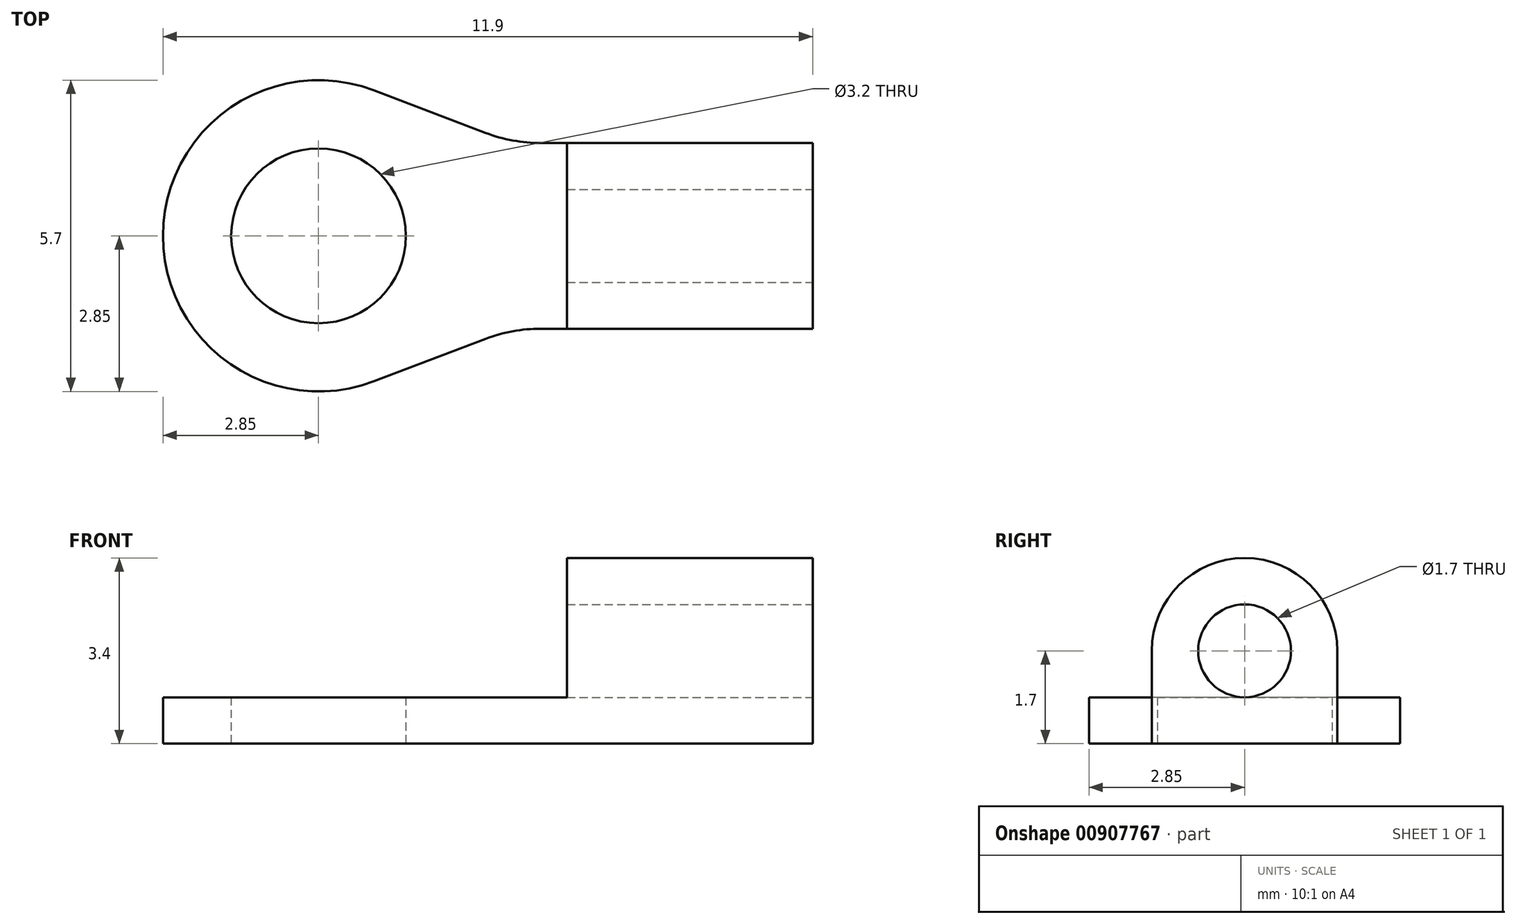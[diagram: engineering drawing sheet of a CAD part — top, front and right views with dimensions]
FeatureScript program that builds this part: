
annotation { "Feature Type Name" : "Feature", "Feature Type Description" : "" }
export const myFeature = defineFeature(function(context is Context, id is Id, definition is map)
    precondition{}
    {
        {
            var Q0;
            Q0=qCreatedBy(makeId("Top.planeOp"),FACE);
            var sketch = newSketch(context, id + "F0", { "sketchPlane" : qUnion([Q0])});
            skLineSegment(sketch, "E0.left", {"start": v(0, 2.85) * mm, "end": v(0, 2.85) * mm});
            skLineSegment(sketch, "E0.right", {"start": v(11.9, 1.15) * mm, "end": v(11.9, 4.55) * mm});
            skPoint(sketch, "E1.visualSharp", {"position": v(0, 5.7) * mm});
            skArc(sketch, "E1.filletArc", {"start": v(2.85, 5.7) * mm, "mid": v(0.83, 4.87) * mm, "end": v(0, 2.85) * mm});
            skPoint(sketch, "E2.visualSharp", {"position": v(0, 0) * mm});
            skArc(sketch, "E2.filletArc", {"start": v(0, 2.85) * mm, "mid": v(0.83, 0.83) * mm, "end": v(2.85, 0) * mm});
            skLineSegment(sketch, "E3.bottom", {"start": v(6.92, 4.55) * mm, "end": v(11.9, 4.55) * mm});
            skLineSegment(sketch, "E3.top", {"start": v(6.92, 1.15) * mm, "end": v(11.9, 1.15) * mm});
            skPoint(sketch, "E3.middle", {"position": v(11.9, 2.85) * mm});
            skArc(sketch, "E4", {"start": v(3.86, 5.51) * mm, "mid": v(0, 2.85) * mm, "end": v(3.86, 0.19) * mm});
            skCircle(sketch, "E5", {"center": v(2.85, 2.85) * mm, "radius": 1.6 * mm});
            skLineSegment(sketch, "E6", {"start": v(5.91, 4.74) * mm, "end": v(3.86, 5.51) * mm});
            skLineSegment(sketch, "E7", {"start": v(5.91, 0.96) * mm, "end": v(3.86, 0.19) * mm});
            skPoint(sketch, "E8.visualSharp", {"position": v(6.4, 4.55) * mm});
            skArc(sketch, "E8.filletArc", {"start": v(5.91, 4.74) * mm, "mid": v(6.4, 4.6) * mm, "end": v(6.92, 4.55) * mm});
            skPoint(sketch, "E9.visualSharp", {"position": v(6.4, 1.15) * mm});
            skArc(sketch, "E9.filletArc", {"start": v(6.92, 1.15) * mm, "mid": v(6.4, 1.1) * mm, "end": v(5.91, 0.96) * mm});
            skPoint(sketch, "E10.orphan", {"position": v(16.4, 4.55) * mm});
            skPoint(sketch, "E11.orphan", {"position": v(16.4, 1.15) * mm});
            skPoint(sketch, "E12.orphan", {"position": v(11.9, 0) * mm});
            skPoint(sketch, "E13.orphan", {"position": v(11.9, 5.7) * mm});
            skPoint(sketch, "E14.orphan", {"position": v(7.4, 4.55) * mm});
            skPoint(sketch, "E15.start.orphan", {"position": v(7.4, 1.15) * mm});
            skSolve(sketch);
        }
        {
            var Q0;
            Q0 = qSketchRegion(id + "F0", true);
            extrude(context, id + "F1", {"entities" : qUnion([Q0]), "depth" : 0.85 * mm, "offsetDistance" : 25 * mm});
        }
        {
            var Q0;
            Q0=makeQuery(id+"F1.opExtrude","CAP_FACE",FACE,{"disambiguationData":[OSD([sQuery(id+"F0.wireOp",EDGE,"E0.right"),sQuery(id+"F0.wireOp",EDGE,"E3.bottom"),sQuery(id+"F0.wireOp",EDGE,"E3.top"),sQuery(id+"F0.wireOp",EDGE,"E4"),sQuery(id+"F0.wireOp",EDGE,"E5"),sQuery(id+"F0.wireOp",EDGE,"E6"),sQuery(id+"F0.wireOp",EDGE,"E7"),sQuery(id+"F0.wireOp",EDGE,"E8.filletArc"),sQuery(id+"F0.wireOp",EDGE,"E9.filletArc")])],"isStart":false});
            var sketch = newSketch(context, id + "F2", { "sketchPlane" : qUnion([Q0])});
            skLineSegment(sketch, "E16.bottom", {"start": v(11.9, 4.55) * mm, "end": v(7.4, 4.55) * mm});
            skLineSegment(sketch, "E16.top", {"start": v(11.9, 1.15) * mm, "end": v(7.4, 1.15) * mm});
            skLineSegment(sketch, "E16.left", {"start": v(11.9, 4.55) * mm, "end": v(11.9, 1.15) * mm});
            skLineSegment(sketch, "E16.right", {"start": v(7.4, 4.55) * mm, "end": v(7.4, 1.15) * mm});
            skSolve(sketch);
        }
        {
            var Q0;
            Q0=makeQuery(id+"F2.imprint","IMPRINT",FACE,{"disambiguationData":[TD([[makeQuery(id+"F2.imprint","IMPRINT",EDGE,{"derivedFrom":sQuery(id+"F2.wireOp",EDGE,"E16.bottom")}),-1.0]])]});
            extrude(context, id + "F3", {"entities" : qUnion([Q0]), "operationType" : NewBodyOperationType.ADD, "depth" : 2.55 * mm, "offsetDistance" : 25 * mm});
        }
        {
            var Q0;
            Q0=makeQuery(id+"F3.opExtrude","CAP_EDGE",EDGE,{"disambiguationData":[OSD([sQuery(id+"F2.wireOp",EDGE,"E16.bottom")])],"isStart":false});
            var Q1;
            Q1=makeQuery(id+"F3.opExtrude","CAP_EDGE",EDGE,{"disambiguationData":[OSD([sQuery(id+"F2.wireOp",EDGE,"E16.top")])],"isStart":false});
            fillet(context, id + "F4", {"entities" : qUnion([Q0, Q1]), "radius" : 1.7 * mm, "tangentPropagation" : true, "allowEdgeOverflow" : false});
        }
        {
            var Q0;
            Q0=makeQuery(id+"F3.boolean.opBoolean","MERGE",FACE,{"derivedFrom":[makeQuery(id+"F1.opExtrude","SWEPT_FACE",FACE,{"disambiguationData":[OSD([sQuery(id+"F0.wireOp",EDGE,"E0.right")])]}),makeQuery(id+"F3.opExtrude","SWEPT_FACE",FACE,{"disambiguationData":[OSD([sQuery(id+"F2.wireOp",EDGE,"E16.left")])]})]});
            var sketch = newSketch(context, id + "F5", { "sketchPlane" : qUnion([Q0])});
            skCircle(sketch, "E17", {"center": v(2.85, 1.7) * mm, "radius": 0.85 * mm});
            skSolve(sketch);
        }
        {
            var Q0;
            Q0=makeQuery(id+"F5.imprint","IMPRINT",FACE,{"disambiguationData":[TD([[makeQuery(id+"F5.imprint","IMPRINT",EDGE,{"derivedFrom":sQuery(id+"F5.wireOp",EDGE,"E17")}),1.0]])]});
            extrude(context, id + "F6", {"entities" : qUnion([Q0]), "operationType" : NewBodyOperationType.REMOVE, "oppositeDirection" : true, "depth" : 25 * mm, "offsetDistance" : 25 * mm});
        }
    });
